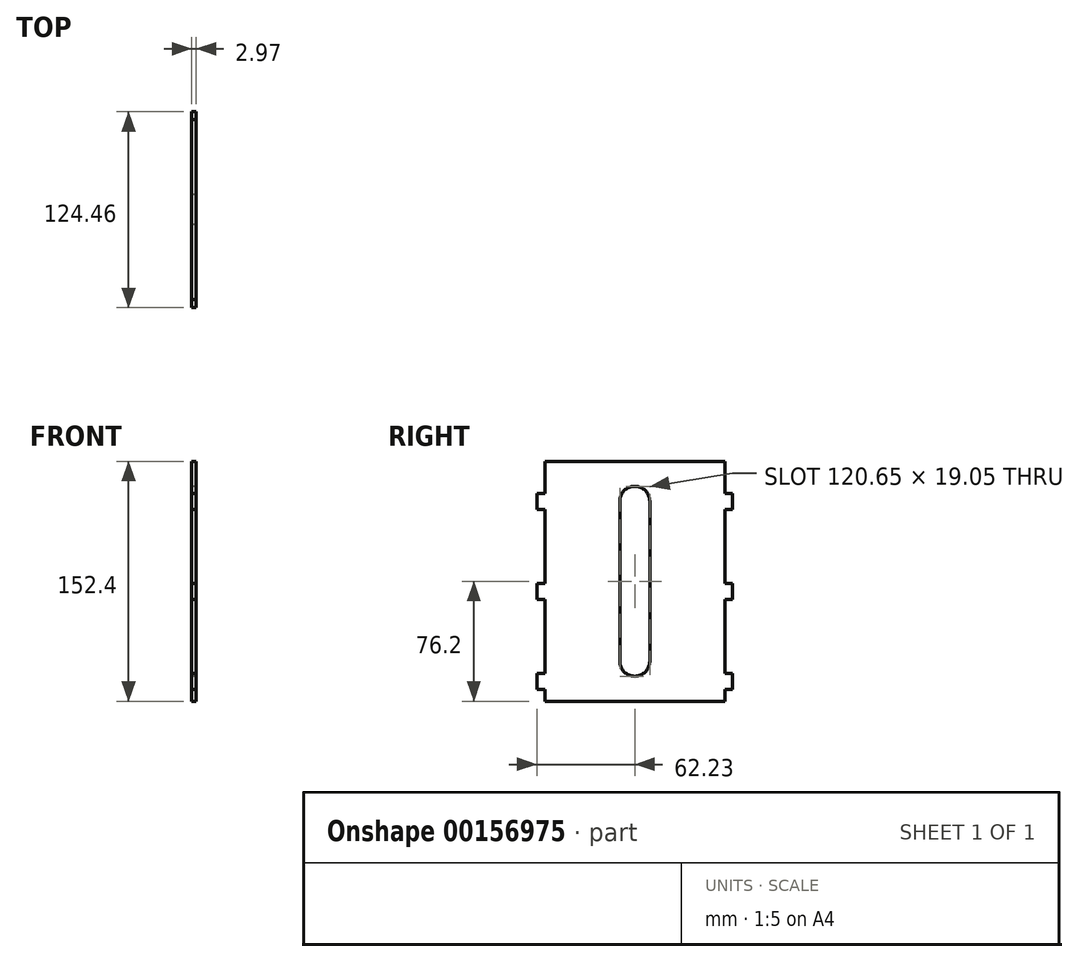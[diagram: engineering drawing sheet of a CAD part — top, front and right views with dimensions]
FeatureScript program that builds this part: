
annotation { "Feature Type Name" : "Feature", "Feature Type Description" : "" }
export const myFeature = defineFeature(function(context is Context, id is Id, definition is map)
    precondition{}
    {
        {
            var Q0;
            Q0=qCreatedBy(makeId("Right.planeOp"),FACE);
            var sketch = newSketch(context, id + "F0", { "sketchPlane" : qUnion([Q0])});
            skLineSegment(sketch, "E0.bottom", {"start": v(57.15, 76.2) * mm, "end": v(-57.15, 76.2) * mm});
            skLineSegment(sketch, "E0.top", {"start": v(57.15, -76.2) * mm, "end": v(-57.15, -76.2) * mm});
            skLineSegment(sketch, "E0.left", {"start": v(57.15, 76.2) * mm, "end": v(57.15, -76.2) * mm});
            skLineSegment(sketch, "E0.right", {"start": v(-57.15, 76.2) * mm, "end": v(-57.15, -76.2) * mm});
            skPoint(sketch, "E0.middle", {"position": v(0, 0) * mm});
            skLineSegment(sketch, "E1.bottom", {"start": v(-38.1, 66.04) * mm, "end": v(38.1, 66.04) * mm});
            skLineSegment(sketch, "E1.top", {"start": v(-38.1, -66.04) * mm, "end": v(38.1, -66.04) * mm});
            skLineSegment(sketch, "E1.left", {"start": v(-38.1, 66.04) * mm, "end": v(-38.1, -66.04) * mm});
            skLineSegment(sketch, "E1.right", {"start": v(38.1, 66.04) * mm, "end": v(38.1, -66.04) * mm});
            skLineSegment(sketch, "E2", {"start": v(0, 50.8) * mm, "end": v(0, -50.8) * mm, "construction": true});
            skArc(sketch, "E3.0.startCap", {"start": v(-9.53, 50.8) * mm, "mid": v(0, 60.33) * mm, "end": v(9.53, 50.8) * mm});
            skArc(sketch, "E3.0.endCap", {"start": v(9.53, -50.8) * mm, "mid": v(0, -60.33) * mm, "end": v(-9.53, -50.8) * mm});
            skLineSegment(sketch, "E3.0.left", {"start": v(9.53, 50.8) * mm, "end": v(9.53, -50.8) * mm});
            skLineSegment(sketch, "E3.0.right", {"start": v(-9.53, 50.8) * mm, "end": v(-9.53, -50.8) * mm});
            skLineSegment(sketch, "E4.bottom", {"start": v(57.15, -68.58) * mm, "end": v(62.23, -68.58) * mm});
            skLineSegment(sketch, "E4.top", {"start": v(57.15, -58.42) * mm, "end": v(62.23, -58.42) * mm});
            skLineSegment(sketch, "E4.left", {"start": v(57.15, -68.58) * mm, "end": v(57.15, -58.42) * mm});
            skLineSegment(sketch, "E4.right", {"start": v(62.23, -68.58) * mm, "end": v(62.23, -58.42) * mm});
            skLineSegment(sketch, "E5.1.0.0", {"start": v(57.15, -11.43) * mm, "end": v(57.15, -1.27) * mm});
            skLineSegment(sketch, "E5.1.0.1", {"start": v(57.15, -1.27) * mm, "end": v(62.23, -1.27) * mm});
            skLineSegment(sketch, "E5.1.0.2", {"start": v(62.23, -11.43) * mm, "end": v(62.23, -1.27) * mm});
            skLineSegment(sketch, "E5.1.0.3", {"start": v(57.15, -11.43) * mm, "end": v(62.23, -11.43) * mm});
            skLineSegment(sketch, "E5.2.0.0", {"start": v(57.15, 45.72) * mm, "end": v(57.15, 55.88) * mm});
            skLineSegment(sketch, "E5.2.0.1", {"start": v(57.15, 55.88) * mm, "end": v(62.23, 55.88) * mm});
            skLineSegment(sketch, "E5.2.0.2", {"start": v(62.23, 45.72) * mm, "end": v(62.23, 55.88) * mm});
            skLineSegment(sketch, "E5.2.0.3", {"start": v(57.15, 45.72) * mm, "end": v(62.23, 45.72) * mm});
            skLineSegment(sketch, "E5.direction1", {"start": v(57.15, -68.58) * mm, "end": v(57.15, -11.43) * mm, "construction": true});
            skLineSegment(sketch, "E6.MirrorCS", {"start": v(-57.15, 55.88) * mm, "end": v(-62.23, 55.88) * mm});
            skLineSegment(sketch, "E7.MirrorCS", {"start": v(-57.15, 45.72) * mm, "end": v(-62.23, 45.72) * mm});
            skLineSegment(sketch, "E8.MirrorCS", {"start": v(-57.15, 45.72) * mm, "end": v(-57.15, 55.88) * mm});
            skLineSegment(sketch, "E9.MirrorCS", {"start": v(-62.23, 45.72) * mm, "end": v(-62.23, 55.88) * mm});
            skLineSegment(sketch, "E10.MirrorCS", {"start": v(-57.15, -1.27) * mm, "end": v(-62.23, -1.27) * mm});
            skLineSegment(sketch, "E11.MirrorCS", {"start": v(-62.23, -11.43) * mm, "end": v(-62.23, -1.27) * mm});
            skLineSegment(sketch, "E12.MirrorCS", {"start": v(-57.15, -11.43) * mm, "end": v(-62.23, -11.43) * mm});
            skLineSegment(sketch, "E13.MirrorCS", {"start": v(-57.15, -11.43) * mm, "end": v(-57.15, -1.27) * mm});
            skLineSegment(sketch, "E14.MirrorCS", {"start": v(-57.15, -58.42) * mm, "end": v(-62.23, -58.42) * mm});
            skLineSegment(sketch, "E15.MirrorCS", {"start": v(-62.23, -68.58) * mm, "end": v(-62.23, -58.42) * mm});
            skLineSegment(sketch, "E16.MirrorCS", {"start": v(-57.15, -68.58) * mm, "end": v(-62.23, -68.58) * mm});
            skLineSegment(sketch, "E17.MirrorCS", {"start": v(-57.15, -68.58) * mm, "end": v(-57.15, -11.43) * mm, "construction": true});
            skSolve(sketch);
        }
        {
            var Q0;
            Q0 = qSketchRegion(id + "F0", true);
            var Q1;
            Q1=makeQuery(id+"F0.imprint","IMPRINT",FACE,{"disambiguationData":[TD([[makeQuery(id+"F0.imprint","IMPRINT",EDGE,{"derivedFrom":sQuery(id+"F0.wireOp",EDGE,"E1.bottom")}),-1.0]])]});
            extrude(context, id + "F1", {"entities" : qUnion([Q0, Q1]), "depth" : 2.97 * mm});
        }
    });
